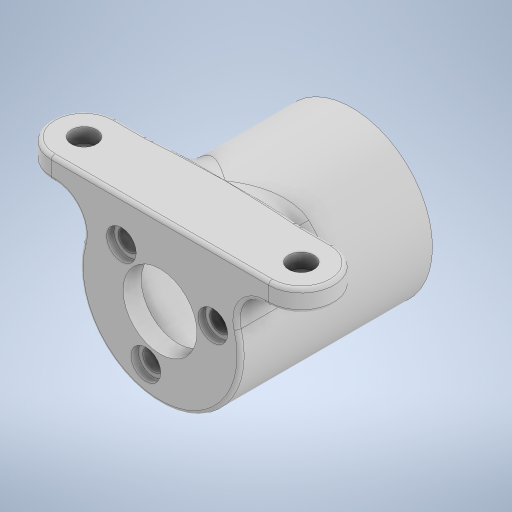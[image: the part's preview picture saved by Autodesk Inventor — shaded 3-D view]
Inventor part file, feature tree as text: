
AUTODESK INVENTOR PART (.ipt)
format: ipt  version: 2024.2 (Build 282272000, 272)  size: 420,352 bytes
history: native  units: mm
features: sketch x7, extrude x5, hole x2, fillet x2, plane x1, chamfer x1
ambient origin geometry x8: Origin, YZ Plane, XZ Plane, XY Plane, X Axis, Y Axis, Z Axis, Center Point
bodies: Solid1 (feature_tree)
feature tree (18):
  extrude  "Extrusion1"  Depth=2.9mm
  extrude  "Extrusion2"  Depth=30.0mm TaperAngle=360.0deg
  extrude  "Extrusion3"  Depth=22.25mm
  plane  "Work Plane1"
  extrude  "Extrusion4"  Depth=4.1mm
  extrude  "Extrusion5"  Depth=20.25mm
  hole  "Hole1"  [1 undecoded]
  hole  "Hole2"  [1 undecoded]
  fillet  "Fillet1"  Radius=15.0mm
  fillet  "Fillet2"  Radius=3.0mm
  chamfer  "Chamfer1"  Distance=1.5mm
  sketch  "Sketch1"  dims[d0=10.2mm d1=2.9mm]
  sketch  "Sketch2"  dims[d2=7.55mm d3=30.0mm d5=360.0deg]
  sketch  "Sketch3"  dims[d7=75.0deg d8=22.25mm]
  sketch  "Sketch4"  dims[d9=1.5mm d10=0.0mm d11=4.1mm]
  sketch  "Sketch5"  dims[d12=1.0mm d13=0.0mm d14=20.25mm]
  sketch  "Sketch6"  dims[d15=24.0mm d16=0.0mm d17=11.125mm]
  sketch  "Sketch7"  dims[d18=9.0mm d19=30.0mm d20=15.0mm d21=3.0mm d22=0.0mm d23=1.5mm d24=0.0mm d25=2.9mm d26=6.0mm d27=4.1mm d28=1.0mm d29=90.0deg d30=8.0mm d31=20.594885mm d32=3.5mm d33=6.0mm d34=5.25mm d35=1.0mm d36=90.0deg d37=8.0mm d38=20.594885mm d39=4.0mm d40=0.5mm d41=0.5mm d42=2.0mm d43=45.0deg]
note: 2 required parameter values undecoded (feature->parameter linkage not recoverable at this tier; creation-order binding heuristic only, values carry confidence <= 0.55)
